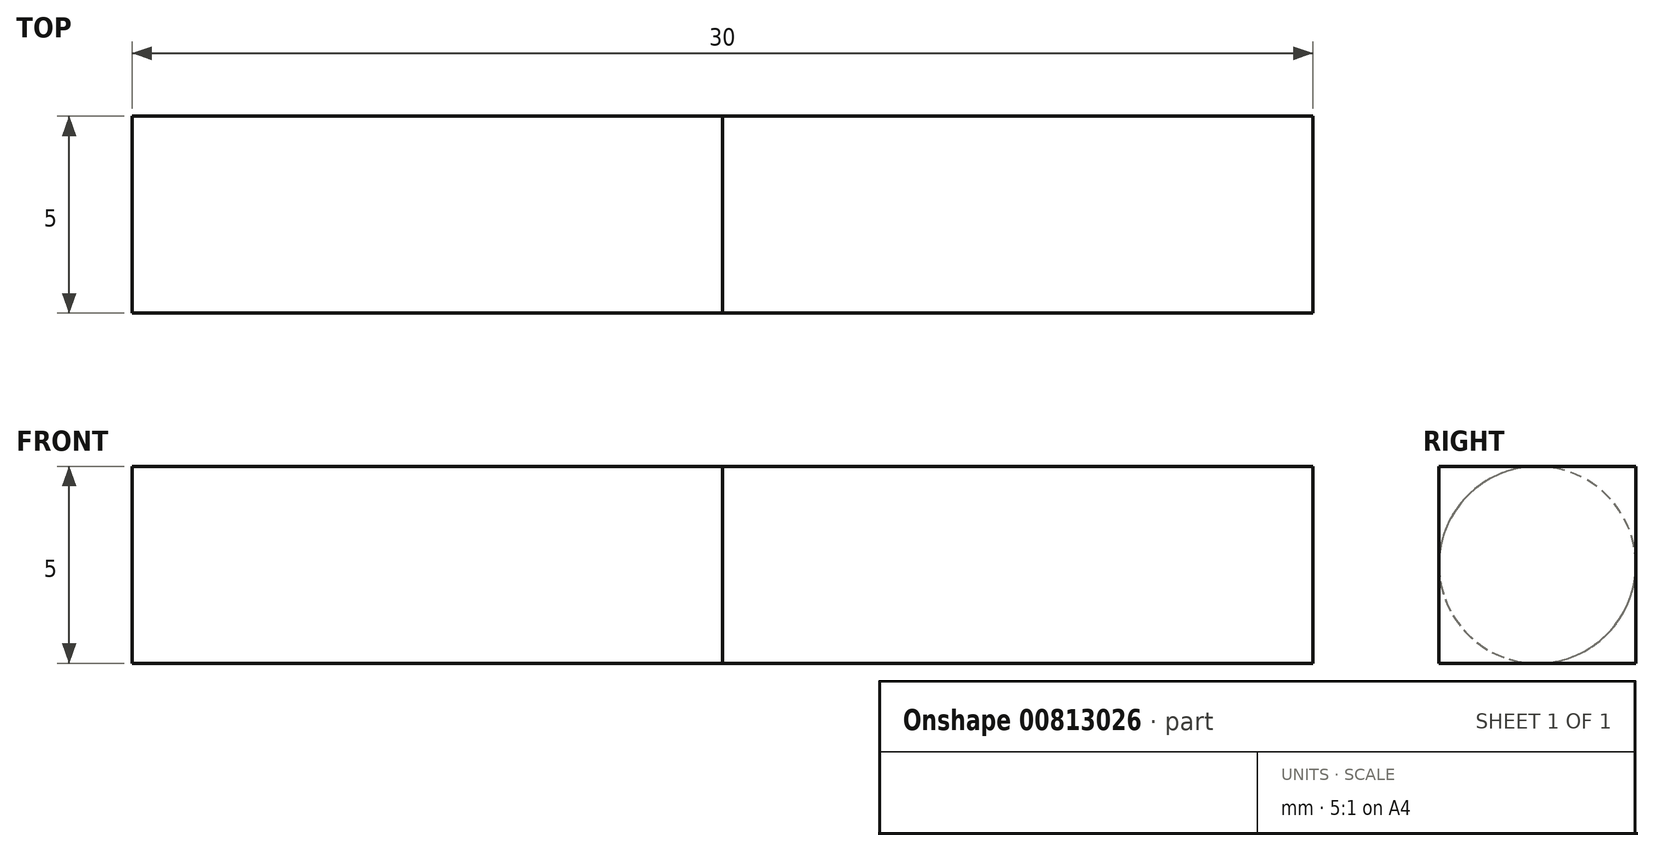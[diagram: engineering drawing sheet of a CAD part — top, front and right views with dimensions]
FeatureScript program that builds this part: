
annotation { "Feature Type Name" : "Feature", "Feature Type Description" : "" }
export const myFeature = defineFeature(function(context is Context, id is Id, definition is map)
    precondition{}
    {
        {
            var Q0;
            Q0=qCreatedBy(makeId("Right.planeOp"),FACE);
            var sketch = newSketch(context, id + "F0", { "sketchPlane" : qUnion([Q0])});
            skCircle(sketch, "E0", {"center": v(0, 0) * mm, "radius": 2.5 * mm});
            skSolve(sketch);
        }
        {
            var Q0;
            Q0 = qSketchRegion(id + "F0", true);
            extrude(context, id + "F1", {"entities" : qUnion([Q0]), "depth" : 15 * mm, "offsetDistance" : 25 * mm});
        }
        {
            var Q0;
            Q0=makeQuery(id+"F1.opExtrude","CAP_FACE",FACE,{"disambiguationData":[OSD([sQuery(id+"F0.wireOp",EDGE,"E0")])],"isStart":false});
            var sketch = newSketch(context, id + "F2", { "sketchPlane" : qUnion([Q0])});
            skLineSegment(sketch, "E1.bottom", {"start": v(-2.5, 2.5) * mm, "end": v(2.5, 2.5) * mm});
            skLineSegment(sketch, "E1.top", {"start": v(-2.5, -2.5) * mm, "end": v(2.5, -2.5) * mm});
            skLineSegment(sketch, "E1.left", {"start": v(-2.5, 2.5) * mm, "end": v(-2.5, -2.5) * mm});
            skLineSegment(sketch, "E1.right", {"start": v(2.5, 2.5) * mm, "end": v(2.5, -2.5) * mm});
            skSolve(sketch);
        }
        {
            var Q0;
            Q0 = qSketchRegion(id + "F2", true);
            extrude(context, id + "F3", {"entities" : qUnion([Q0]), "operationType" : NewBodyOperationType.ADD, "depth" : 15 * mm, "offsetDistance" : 25 * mm});
        }
    });
